# Revit family: SPECTRA SIDE FIX
name_source: partatom
category: Generic Models
units: mm (PartAtom-declared; Revit-internal decimal feet)

## family parameters
Always vertical = No
Can host rebar = No
Cut with Voids When Loaded = No
Part Type = Normal
Room Calculation Point = No
Round Connector Dimension = Use Diameter
Shared = No
Work Plane-Based = No

## types (5) — shared parameters
HEIGHT = 1100 mm
Keynote = UNEX SYSTEMS, CAMDEN SIDE FIX BALUSTRADE
LENGTH = 2500 mm  [stored 8.2021 ft]
Manufacturer = UNEX SYSTEMS
Max Post Spacing = 1000 mm  [stored 3.28084 ft]
Pannel QTY = 3
Post Height = 1076 mm  [stored 3.53018 ft]
Post QTY = 4
Top Rail Height = 24 mm  [stored 0.0787402 ft]
UNDER SPACE = 200 mm  [stored 0.656168 ft]
zero-valued in all types: Default Elevation

## per-type parameters (varying)
| type | ART TOP RAIL | Description | Model | PPR TOP RAIL | URL | VRE TOP RAIL | VRR TOP RAIL | VRT TOP RAIL |
| SPECTRA WITH VRE (SIDE FIX) | No | UNEX CAMDEN FRAMED GLASS WITH VRE TOP RAIL | UNEX, CAMDEN SIDE FIX (VRE) | No | WWW.UNEX.CO.NZ | Yes | No | No |
| SPECTRA WITH PRR (SIDE FIX) | No | UNEX CAMDEN FRAMED GLASS WITH PRR TOP RAIL | UNEX, CAMDEN SIDE FIX (PRR) | Yes | WWW.UNEX.CO.NZ
WWW.UNEX.CO.NZ
WWW.UNEX.CO.NZ | No | No | No |
| SPECTRA WITH ART (SIDE FIX) | Yes | UNEX CAMDEN FRAMED GLASS WITH ART TOP RAIL | UNEX, CAMDEN SIDE FIX (ART) | No | WWW.UNEX.CO.NZ | No | No | No |
| SPECTRA WITH VRT (SIDE FIX) | No | UNEX CAMDEN FRAMED GLASS WITH VRT TOP RAIL | UNEX, CAMDEN SIDE FIX (VRT) | No | WWW.UNEX.CO.NZ | No | No | Yes |
| SPECTRA WITH VRR (SIDE FIX) | No | UNEX CAMDEN FRAMED GLASS WITH VRR TOP RAIL | UNEX, CAMDEN SIDE FIX (VRR) | No | WWW.UNEX.CO.NZ | No | Yes | No |

note: [stored X ft] marks values corroborated as IEEE doubles in the binary element streams (Revit-internal decimal feet)

## geometry (parser evidence)
native form markers: Blend x2, Sweep x25
no freeform markers — native parametric forms only
